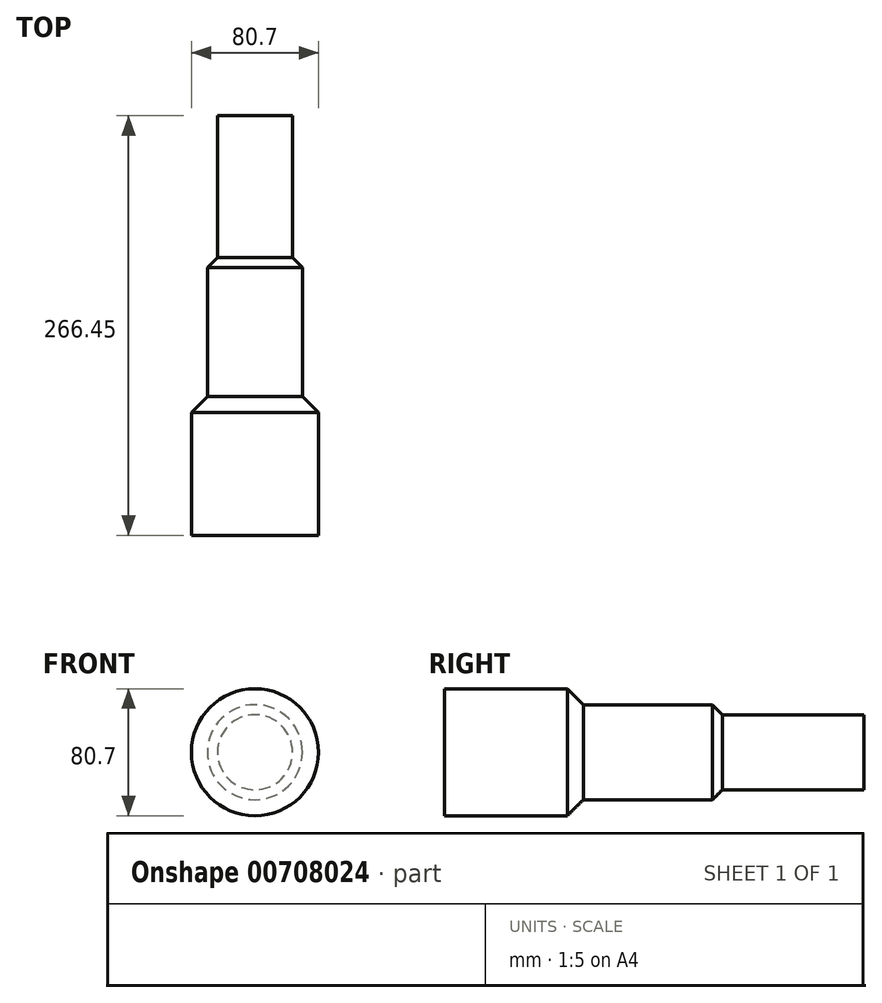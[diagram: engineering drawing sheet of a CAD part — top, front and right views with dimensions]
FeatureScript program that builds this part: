
annotation { "Feature Type Name" : "Feature", "Feature Type Description" : "" }
export const myFeature = defineFeature(function(context is Context, id is Id, definition is map)
    precondition{}
    {
        {
            var Q0;
            Q0=qCreatedBy(makeId("Front.planeOp"),FACE);
            var sketch = newSketch(context, id + "F0", { "sketchPlane" : qUnion([Q0])});
            skCircle(sketch, "E0", {"center": v(0, 0) * mm, "radius": 40.35 * mm});
            skSolve(sketch);
        }
        {
            var Q0;
            Q0 = qSketchRegion(id + "F0", true);
            var Q1;
            Q1=makeQuery(id+"F0.imprint","IMPRINT",FACE,{"disambiguationData":[TD([[makeQuery(id+"F0.imprint","IMPRINT",EDGE,{"derivedFrom":sQuery(id+"F0.wireOp",EDGE,"E0")}),1.0]])]});
            extrude(context, id + "F1", {"entities" : qUnion([Q0, Q1]), "oppositeDirection" : true, "depth" : 88.14 * mm, "offsetDistance" : 25.4 * mm});
        }
        {
            var Q0;
            Q0=makeQuery(id+"F1.opExtrude","CAP_EDGE",EDGE,{"disambiguationData":[OSD([sQuery(id+"F0.wireOp",EDGE,"E0")])],"isStart":false});
            chamfer(context, id + "F2", {"entities" : qUnion([Q0]), "width" : 10.16 * mm, "tangentPropagation" : true});
        }
        {
            var Q0;
            Q0=makeQuery(id+"F1.opExtrude","CAP_FACE",FACE,{"disambiguationData":[OSD([sQuery(id+"F0.wireOp",EDGE,"E0")])],"isStart":false});
            extrude(context, id + "F3", {"entities" : qUnion([Q0]), "operationType" : NewBodyOperationType.ADD, "depth" : 88.4 * mm, "offsetDistance" : 25.4 * mm});
        }
        {
            var Q0;
            Q0=makeQuery(id+"F3.opExtrude","CAP_EDGE",EDGE,{"disambiguationData":[OSD([sQuery(id+"F0.wireOp",EDGE,"E0")])],"isStart":false});
            chamfer(context, id + "F4", {"entities" : qUnion([Q0]), "width" : 6.35 * mm, "tangentPropagation" : true});
        }
        {
            var Q0;
            Q0=makeQuery(id+"F3.opExtrude","CAP_FACE",FACE,{"disambiguationData":[OSD([sQuery(id+"F0.wireOp",EDGE,"E0")])],"isStart":false});
            extrude(context, id + "F5", {"entities" : qUnion([Q0]), "operationType" : NewBodyOperationType.ADD, "depth" : 89.92 * mm, "offsetDistance" : 25.4 * mm});
        }
    });
